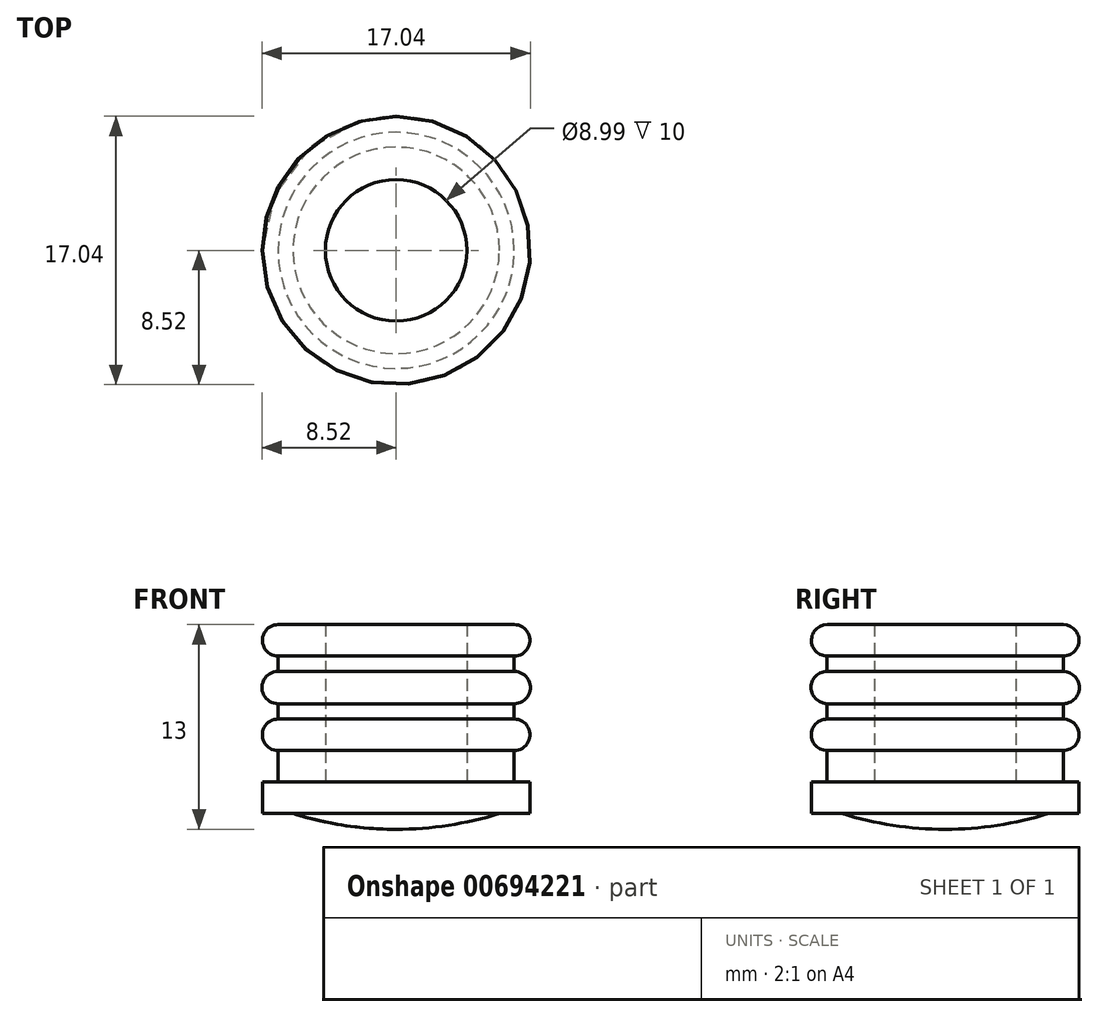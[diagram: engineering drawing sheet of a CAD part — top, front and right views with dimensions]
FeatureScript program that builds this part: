
annotation { "Feature Type Name" : "Feature", "Feature Type Description" : "" }
export const myFeature = defineFeature(function(context is Context, id is Id, definition is map)
    precondition{}
    {
        {
            var Q0;
            Q0=qCreatedBy(makeId("Front.planeOp"),FACE);
            var sketch = newSketch(context, id + "F0", { "sketchPlane" : qUnion([Q0])});
            skLineSegment(sketch, "E0", {"start": v(0, -27.41) * mm, "end": v(0, 37.74) * mm, "construction": true});
            skLineSegment(sketch, "E1", {"start": v(0, 0) * mm, "end": v(0, 13) * mm, "construction": true});
            skLineSegment(sketch, "E2", {"start": v(0, 13) * mm, "end": v(0, 3) * mm, "construction": true});
            skLineSegment(sketch, "E3", {"start": v(8.5, 3) * mm, "end": v(8.5, 1) * mm});
            skLineSegment(sketch, "E4", {"start": v(8.5, 1) * mm, "end": v(6.5, 1) * mm});
            skLineSegment(sketch, "E5", {"start": v(8.5, 3) * mm, "end": v(7.5, 3) * mm});
            skArc(sketch, "E6", {"start": v(7.5, 7.98) * mm, "mid": v(8.52, 9) * mm, "end": v(7.5, 10.02) * mm});
            skArc(sketch, "E7", {"start": v(7.5, 5) * mm, "mid": v(8.5, 6) * mm, "end": v(7.5, 7) * mm});
            skArc(sketch, "E8", {"start": v(7.5, 11) * mm, "mid": v(8.5, 12) * mm, "end": v(7.5, 13) * mm});
            skLineSegment(sketch, "E9", {"start": v(7.5, 11) * mm, "end": v(7.5, 10.02) * mm});
            skLineSegment(sketch, "E10", {"start": v(7.5, 7.98) * mm, "end": v(7.5, 7) * mm});
            skLineSegment(sketch, "E11", {"start": v(7.5, 5) * mm, "end": v(7.5, 3) * mm});
            skLineSegment(sketch, "E12", {"start": v(0, 0) * mm, "end": v(0, 19) * mm, "construction": true});
            skLineSegment(sketch, "E13", {"start": v(7.5, 13) * mm, "end": v(4.5, 13) * mm});
            skLineSegment(sketch, "E14", {"start": v(4.5, 13) * mm, "end": v(4.5, 3) * mm});
            skLineSegment(sketch, "E15", {"start": v(4.5, 3) * mm, "end": v(0, 3) * mm});
            skLineSegment(sketch, "E16", {"start": v(0, 3) * mm, "end": v(0, 0) * mm});
            skLineSegment(sketch, "E17", {"start": v(0, 0) * mm, "end": v(0, 22) * mm, "construction": true});
            skArc(sketch, "E18", {"start": v(0, 0) * mm, "mid": v(3.32, 0.25) * mm, "end": v(6.56, 1) * mm});
            skSolve(sketch);
        }
        {
            var Q0;
            {var subQ0=sQuery(id+"F0.wireOp",EDGE,"E3");Q0=makeQuery(id+"F0.imprint","IMPRINT",FACE,{"disambiguationData":[TD([[makeQuery(id+"F0.imprint","IMPRINT",EDGE,{"derivedFrom":subQ0}),-1.0]])]});}
            var Q1;
            Q1=sQuery(id+"F0.wireOp",EDGE,"E12");
            revolve(context, id + "F1", {"entities" : qUnion([Q0]), "axis" : qUnion([Q1]), "revolveType" : RevolveType.FULL});
        }
    });
